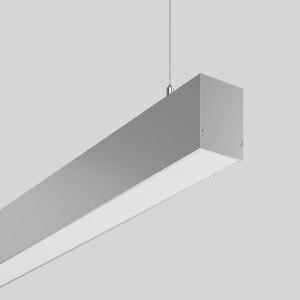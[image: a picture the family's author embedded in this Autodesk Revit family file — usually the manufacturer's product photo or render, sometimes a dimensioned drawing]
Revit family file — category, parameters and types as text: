
# Revit family: less_is_more_50_312321_0045_1_aeac
name_source: partatom
category: Lighting Fixtures
units: mm (PartAtom-declared; Revit-internal decimal feet)

## family parameters
Cut with Voids When Loaded = No
Host = Face
Light Source = No
Part Type = Normal
Room Calculation Point = No
Round Connector Dimension = Use Diameter
Shared = No

## types (1)
- LESS IS MORE 50 (1 x LED Modul 840, 8850 lm, 4000)
    Apparent Load = 74 VA
    CIE Flux Codes = 49 80 96 63 100
    Color Rendering = 80
    Color Temperature = 4000
    Default Elevation = 1800 mm
    Description = Series: LESS IS MORE 50
Linear pendant luminaire for aesthetically sophisticated lighting. Housing: extruded aluminium profile, powder-coated. End cap aluminium powder-coated. Canopy made of aluminium, powder-coated. Diffuser made of non-yellowing plastic (PMMA), opal. Direct 65%, indirect 35% light emission. Suitable for pendant. 2-point steel cable suspension freely positionable and infinitely height-adjustable. Special lengths available on request. LED unit with integrated converter interchangeable and removable. Suitable for through-wiring. With sensors or as a safety luminaire on request. 
Colour: white aluminium (RAL 9006)
Length: 1967 mm
Width: 57 mm
Height: 75 mm
Suspension length: 2000 mm
Lamp: LED
Socket: without socket
Colour temperature: 4000K
Colour rendering index (CRI): 80
Light source: LED
Socket lamp2: Without base
Colour temperature: 4000K
System power: 74 W
Rated luminous flux: 8850 lm
Luminous efficiency: 120 lm/W
Control gear: Regulated power supply
Control gear: Regulated power supply
Protection class: I
Type of protection: IP 20
    Height = 75 mm
    Lamp = 1 x LED Modul 840
    Lamp Light Flux = 8850 lm
    Lamp count = 1
    Length = 1967 mm
    Lifetime = 50000 h
    Luminous efficacy = 120 lm/W
    Manufacturer = RZB
    ModVariant = No
    Model = 312321.0045.1
    Mounting Place = Ceiling
    Mounting Type = Pendant
    Number of Poles = 1
    OnlyDefault = Yes
    Power Factor = 1
    Product Name = LESS IS MORE 50
    Product group = Pendant LED linear luminaires
    ProductGroupID = 907
    Protection Class = Protection class I
    Protection Degree = IP 20
    RLX_Detail_Level = 1
    RLX_Emergency_Light_Flux = 0 lm
    RLX_Emergency_Type = 0
    RLX_Emergency_Type_DB = No
    RlxData = <blob elided: 36373 chars, md5=637233fe>
    Socket = socket
    Standby Power = 0 W
    System Light Flux = 8850 lm
    System Power = 74 W
    Type Comments = Product without accessories
    Type Image = 312318.004.jpg
    URL = http://relux.com
    VarID = ---
    Voltage = 230 V
    Voltage Range = 220-240 V
    Weight = 0.00 kg
    Width = 57 mm

## geometry (parser evidence)
native form markers: Blend x4, Sweep x15
no freeform markers — native parametric forms only
